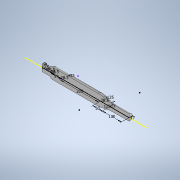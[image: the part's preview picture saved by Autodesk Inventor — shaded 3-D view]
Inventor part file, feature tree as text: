
AUTODESK INVENTOR PART (.ipt)
format: ipt  version: 2022 (Build 260153000, 153)  size: 212,480 bytes
history: native  units: mm
features: sketch x1, revolve x1, extrude x1, fillet x1
ambient origin geometry x8: Origin, YZ Plane, XZ Plane, XY Plane, X Axis, Y Axis, Z Axis, Center Point
bodies: Body1 (feature_tree)
feature tree (4):
  sketch  "Sketch1"  dims[d0=41.0mm d1=6.0mm d2=59.0mm d3=200.0mm d4=50.0mm d5=100.0mm d6=19.5mm d7=19.5mm d8=28.5mm d10=28.5mm d11=17.0mm d12=17.0mm d13=2.0mm d14=8.0mm d16=125.0mm d17=125.0mm d18=2.0mm d25=35.0mm d26=28.5mm d27=180.0deg d28=100.0mm d29=0.0mm d30=2.0mm d19=0.872665mm d20=0.872665mm d31=0.0mm d32=0.0mm d33=0.0mm]
  revolve  "Revolution2"  [1 undecoded]
  extrude  "Extrusion2"  Depth=59.0mm
  fillet  "Fillet1"  Radius=200.0mm
note: 1 required parameter value undecoded (feature->parameter linkage not recoverable at this tier; creation-order binding heuristic only, values carry confidence <= 0.55)
